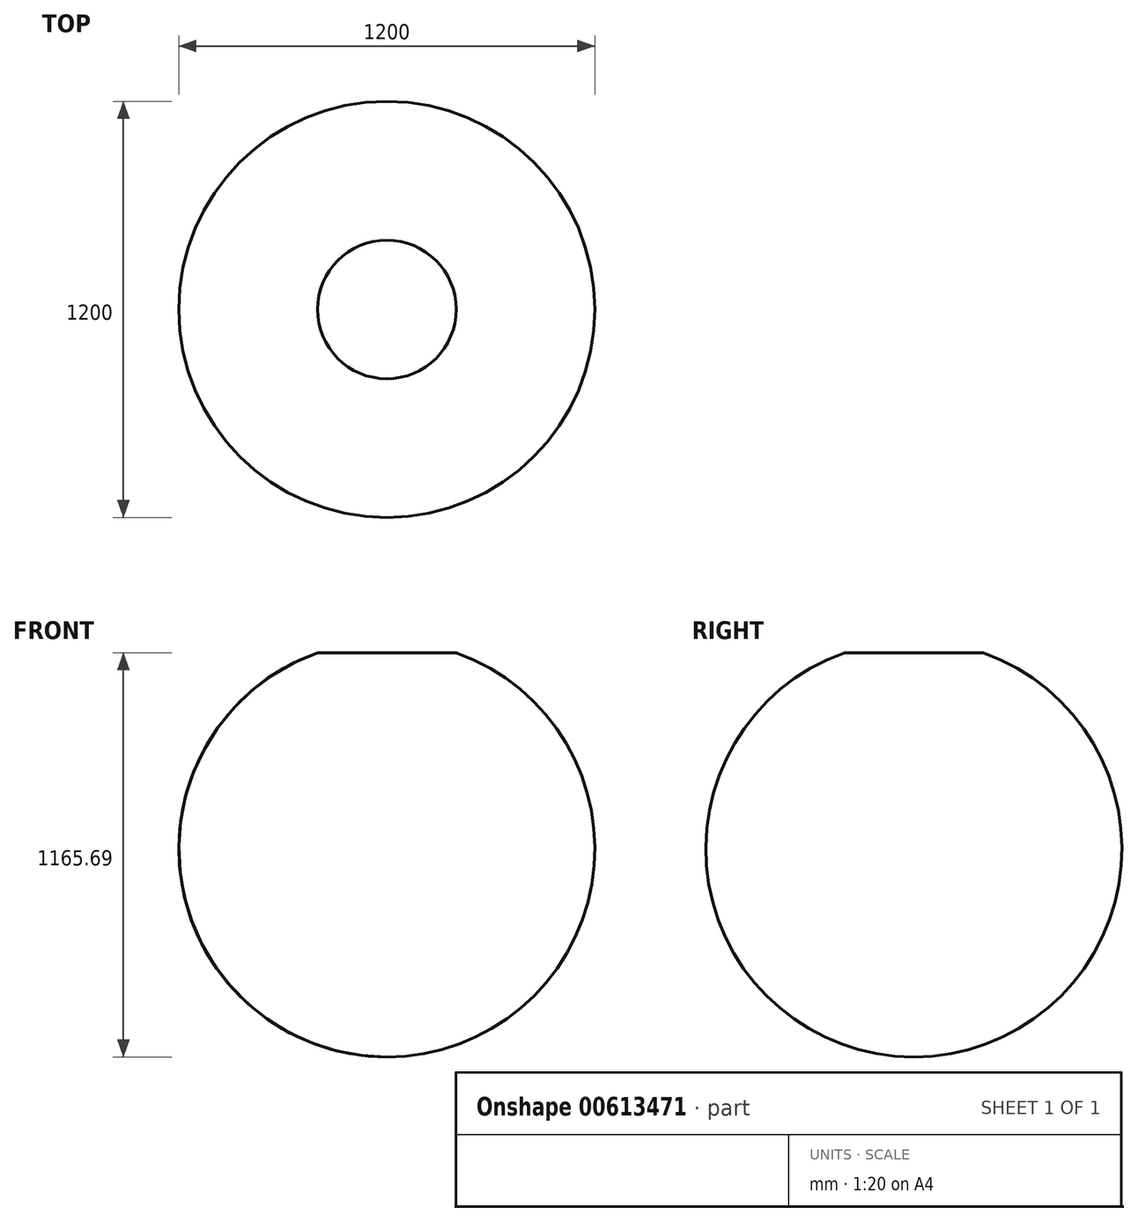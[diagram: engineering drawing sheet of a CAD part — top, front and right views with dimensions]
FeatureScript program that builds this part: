
annotation { "Feature Type Name" : "Feature", "Feature Type Description" : "" }
export const myFeature = defineFeature(function(context is Context, id is Id, definition is map)
    precondition{}
    {
        {
            var Q0;
            Q0=qCreatedBy(makeId("Front.planeOp"),FACE);
            var sketch = newSketch(context, id + "F0", { "sketchPlane" : qUnion([Q0])});
            skPoint(sketch, "E0", {"position": v(0, 0) * mm});
            skLineSegment(sketch, "E1", {"start": v(0, 565.69) * mm, "end": v(0, -600) * mm});
            skLineSegment(sketch, "E2", {"start": v(0, 565.69) * mm, "end": v(200, 565.69) * mm});
            skArc(sketch, "E3", {"start": v(200, 565.69) * mm, "mid": v(591.36, -101.46) * mm, "end": v(0, -600) * mm});
            skSolve(sketch);
        }
        {
            var Q0;
            Q0=makeQuery(id+"F0.imprint","IMPRINT",FACE,{"disambiguationData":[TD([[makeQuery(id+"F0.imprint","IMPRINT",EDGE,{"derivedFrom":sQuery(id+"F0.wireOp",EDGE,"E1")}),1.0]])]});
            var Q1;
            Q1=sQuery(id+"F0.wireOp",EDGE,"E3");
            var Q2;
            Q2=sQuery(id+"F0.wireOp",EDGE,"E1");
            revolve(context, id + "F1", {"bodyType" : ToolBodyType.SURFACE, "entities" : qUnion([Q0]), "surfaceEntities" : qUnion([Q1]), "axis" : qUnion([Q2]), "revolveType" : RevolveType.FULL});
        }
    });
